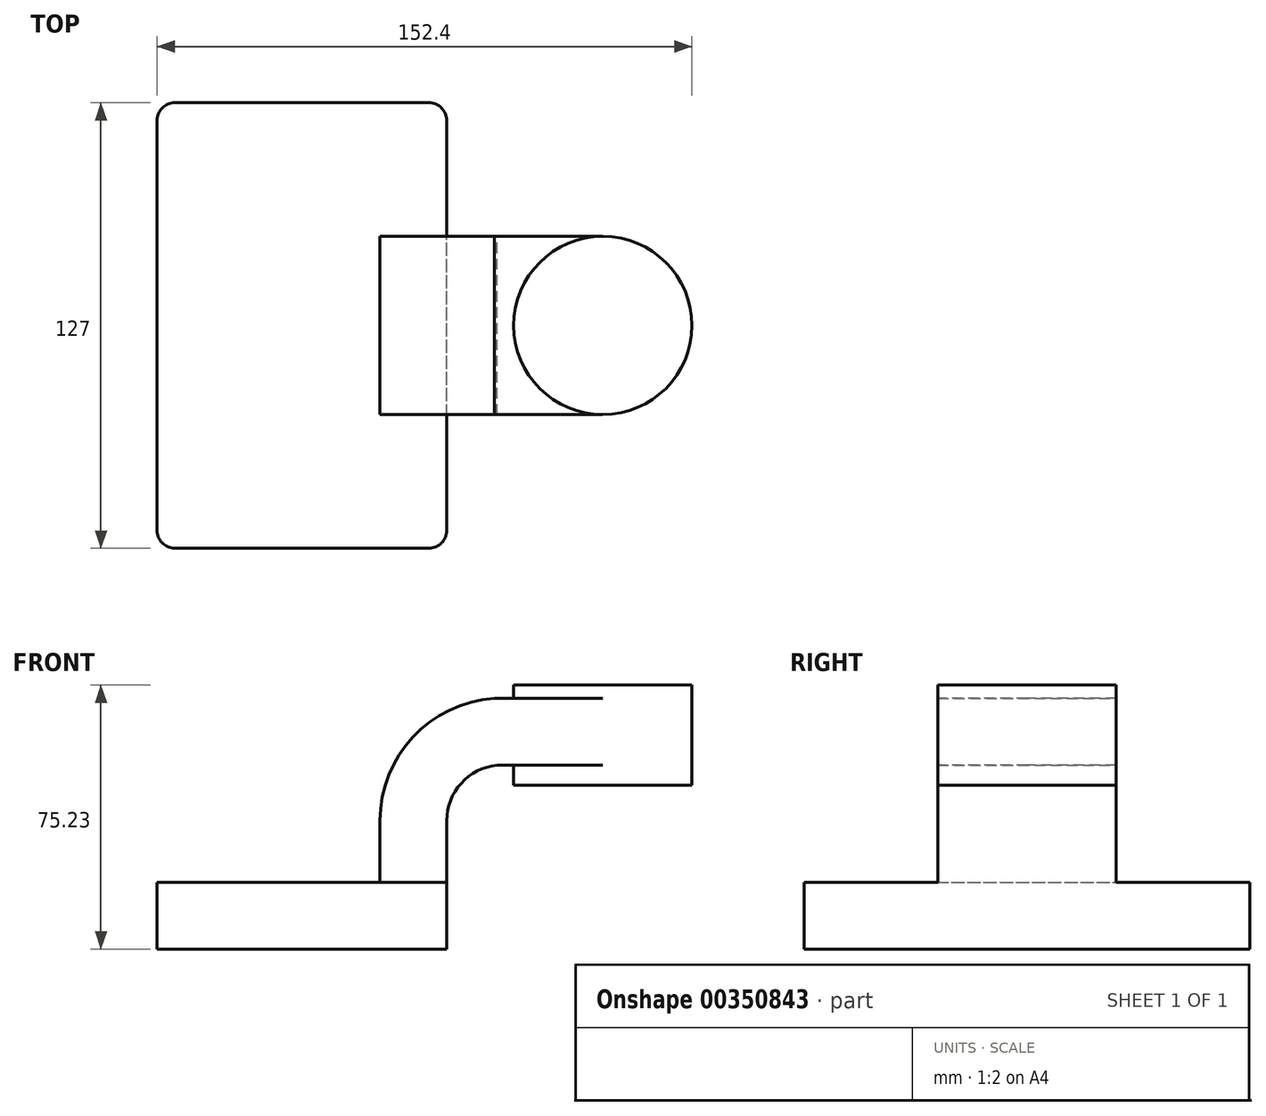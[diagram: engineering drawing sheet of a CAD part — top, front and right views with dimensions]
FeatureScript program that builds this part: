
annotation { "Feature Type Name" : "Feature", "Feature Type Description" : "" }
export const myFeature = defineFeature(function(context is Context, id is Id, definition is map)
    precondition{}
    {
        {
            var Q0;
            Q0=qCreatedBy(makeId("Front.planeOp"),FACE);
            var sketch = newSketch(context, id + "F0", { "sketchPlane" : qUnion([Q0])});
            skLineSegment(sketch, "E0.bottom", {"start": v(41.27, 9.53) * mm, "end": v(-41.28, 9.53) * mm});
            skLineSegment(sketch, "E0.top", {"start": v(41.28, -9.52) * mm, "end": v(-41.27, -9.52) * mm});
            skLineSegment(sketch, "E0.left", {"start": v(41.28, 9.53) * mm, "end": v(41.28, -9.52) * mm});
            skLineSegment(sketch, "E0.right", {"start": v(-41.28, 9.53) * mm, "end": v(-41.27, -9.52) * mm});
            skPoint(sketch, "E0.middle", {"position": v(0, 0) * mm});
            skLineSegment(sketch, "E1.top", {"start": v(111.13, 37.12) * mm, "end": v(60.33, 37.12) * mm});
            skLineSegment(sketch, "E1.left", {"start": v(111.13, 65.7) * mm, "end": v(111.13, 37.12) * mm});
            skLineSegment(sketch, "E1.right", {"start": v(60.33, 65.7) * mm, "end": v(60.33, 37.12) * mm});
            skPoint(sketch, "E1.middle", {"position": v(85.73, 51.4) * mm});
            skLineSegment(sketch, "E2", {"start": v(41.27, 9.53) * mm, "end": v(41.27, 27.07) * mm});
            skArc(sketch, "E3", {"start": v(41.28, 27.07) * mm, "mid": v(45.38, 37.72) * mm, "end": v(55.57, 42.86) * mm});
            skLineSegment(sketch, "E4", {"start": v(55.57, 42.86) * mm, "end": v(85.73, 42.86) * mm});
            skLineSegment(sketch, "E5", {"start": v(60.33, 65.7) * mm, "end": v(111.13, 65.7) * mm});
            skLineSegment(sketch, "E6.0", {"start": v(54.8, 61.91) * mm, "end": v(85.73, 61.91) * mm});
            skArc(sketch, "E6.1", {"start": v(22.23, 27.07) * mm, "mid": v(31.64, 50.92) * mm, "end": v(54.8, 61.91) * mm});
            skLineSegment(sketch, "E6.2", {"start": v(22.23, 9.53) * mm, "end": v(22.23, 27.07) * mm});
            skLineSegment(sketch, "E7", {"start": v(85.73, 37.12) * mm, "end": v(85.73, 65.7) * mm});
            skFitSpline(sketch, "E8", {"points": [v(-41.28, 9.52) * mm, v(54.8, 61.91) * mm], "startDerivative": vector(22.96, 79.12) * mm, "endDerivative": vector(133.35, 8.05) * mm});
            skSolve(sketch);
        }
        {
            var Q0;
            Q0=makeQuery(id+"F0.imprint","IMPRINT",FACE,{"disambiguationData":[TD([[makeQuery(id+"F0.imprint","IMPRINT",EDGE,{"derivedFrom":sQuery(id+"F0.wireOp",EDGE,"E0.top")}),-1.0]])]});
            extrude(context, id + "F1", {"entities" : qUnion([Q0]), "endBound" : BoundingType.SYMMETRIC, "depth" : 127 * mm});
        }
        {
            var Q0;
            {var subQ1=sQuery(id+"F0.wireOp",EDGE,"E2");Q0=makeQuery(id+"F0.imprint","IMPRINT",FACE,{"disambiguationData":[TD([[makeQuery(id+"F0.imprint","IMPRINT",EDGE,{"derivedFrom":subQ1}),1.0]])]});}
            var Q1;
            {var subQ0=sQuery(id+"F0.wireOp",EDGE,"E6.0");var subQ1=sQuery(id+"F0.wireOp",EDGE,"E1.right");var subQ2=makeQuery(id+"F0.imprint","INTERSECT",VERTEX,{"derivedFrom":[subQ1,subQ0]});Q1=makeQuery(id+"F0.imprint","IMPRINT",FACE,{"disambiguationData":[TD([[makeQuery(id+"F0.imprint","IMPRINT",EDGE,{"disambiguationData":[TD([[subQ2,-1.0]])],"derivedFrom":subQ1}),1.0]])]});}
            extrude(context, id + "F2", {"entities" : qUnion([Q0, Q1]), "operationType" : NewBodyOperationType.ADD, "endBound" : BoundingType.SYMMETRIC, "depth" : 50.8 * mm});
        }
        {
            var Q0;
            Q0=makeQuery(id+"F0.imprint","IMPRINT",FACE,{"disambiguationData":[TD([[makeQuery(id+"F0.imprint","IMPRINT",EDGE,{"derivedFrom":sQuery(id+"F0.wireOp",EDGE,"E6.1")}),1.0]])]});
            extrude(context, id + "F3", {"entities" : qUnion([Q0]), "operationType" : NewBodyOperationType.ADD, "endBound" : BoundingType.SYMMETRIC, "depth" : 15.88 * mm});
        }
        {
            var Q0;
            {var subQ5=sQuery(id+"F0.wireOp",EDGE,"E1.left");Q0=makeQuery(id+"F0.imprint","IMPRINT",FACE,{"disambiguationData":[TD([[makeQuery(id+"F0.imprint","IMPRINT",EDGE,{"derivedFrom":subQ5}),-1.0]])]});}
            var Q1;
            Q1=sQuery(id+"F0.wireOp",EDGE,"E7");
            revolve(context, id + "F4", {"operationType" : NewBodyOperationType.ADD, "entities" : qUnion([Q0]), "axis" : qUnion([Q1]), "revolveType" : RevolveType.FULL});
        }
        {
            var Q0;
            Q0=makeQuery(id+"F1.opExtrude","CAP_EDGE",EDGE,{"disambiguationData":[OSD([sQuery(id+"F0.wireOp",EDGE,"E0.left")])],"isStart":false});
            var Q1;
            Q1=makeQuery(id+"F1.opExtrude","CAP_EDGE",EDGE,{"disambiguationData":[OSD([sQuery(id+"F0.wireOp",EDGE,"E0.left")])],"isStart":true});
            var Q2;
            Q2=makeQuery(id+"F1.opExtrude","CAP_EDGE",EDGE,{"disambiguationData":[OSD([sQuery(id+"F0.wireOp",EDGE,"E0.right")])],"isStart":false});
            var Q3;
            Q3=makeQuery(id+"F1.opExtrude","CAP_EDGE",EDGE,{"disambiguationData":[OSD([sQuery(id+"F0.wireOp",EDGE,"E0.right")])],"isStart":true});
            var Q4;
            Q4=makeQuery(id+"F2.opExtrude","SWEPT_EDGE",EDGE,{"disambiguationData":[OSD([sQuery(id+"F0.wireOp",EDGE,"E2"),sQuery(id+"F0.wireOp",EDGE,"E3")])]});
            fillet(context, id + "F5", {"entities" : qUnion([Q0, Q1, Q2, Q3, Q4]), "radius" : 5.08 * mm, "tangentPropagation" : true, "allowEdgeOverflow" : false});
        }
    });
